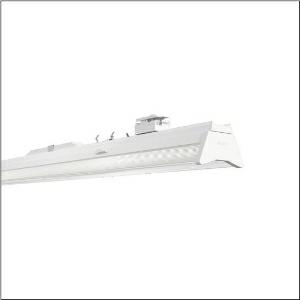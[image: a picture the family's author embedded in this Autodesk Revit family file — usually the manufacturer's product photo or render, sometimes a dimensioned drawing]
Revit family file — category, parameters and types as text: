
# Revit family: licross_r__11_performance_ho_51tm16cn4exm_9d3d
name_source: partatom
category: Lighting Fixtures
units: mm (PartAtom-declared; Revit-internal decimal feet)

## family parameters
Cut with Voids When Loaded = No
Host = Face
Light Source = No
Part Type = Normal
Room Calculation Point = No
Round Connector Dimension = Use Diameter
Shared = No

## types (1)
- --- (1 x LED, 14420 lm, 77.6 W, 4000K)
    Apparent Load = 78 VA
    CIE Flux Codes = 63 87 95 78 100
    Color Rendering = 80
    Color Temperature = 4000K
    Default Elevation = 1800 mm
    Description = Licross® 11 Performance HO, luminaire insert, of sheet steel, galvanised, coil coated, white, length: 1.500mm, width: 120mm, height: 123mm, LED rated luminous flux: 14.420lm, light colour: 840, control gear: ON/OFF Multilumen, CLOi, with plug, 3-pole, with phase selection, mains connection: 220..240V, AC, 50/60Hz, start of lifetime: 78W, end of service life: 87W, internal wiring halogen-free, primary light control with lens, of plastic, primary optical cover: cover, of PMMA, light emission: direct/indirect distribution, primary light characteristic: symmetric, protection rating (complete): IP40, insulation class (complete): insulation class I (protective earthing), certification: CE, ENEC, VDE, UKCA, protection symbol: D if used in an environment without relevant dust loads with corresponding accessories, impact resistance: IK06, permissible ambient temperature for indoor applications: -35..+35°C, corresponds to IFS (International Featured Standards) requirements for safety and quality in the food industry, reducing of maximum allowable ambient temperature of 5°C with ceiling mounting, LABS conformity tested according to VDMA 24364:2018-05, packaging unit: 1 piece
    Height = 114 mm
    Lamp = 1 x LED
    Lamp Light Flux = 14420 lm
    Lamp Power = 77.6 W
    Lamp count = 1
    Length = 1500 mm
    Luminous efficacy = 186 lm/W
    Manufacturer = Siteco
    ModVariant = No
    Model = 51TM16CN4EXM
    Mounting Place = Ceiling
    Mounting Type = Pendant
    Number of Poles = 1
    OnlyDefault = Yes
    Power Factor = 1
    Product Name = Licross® 11 Performance HO
    Product group = luminaire insert | ceiling pendant
    ProductGroupID = 902
    Protection Class = Protection class I
    Protection Degree = IP 40
    RLX_Detail_Level = 1
    RLX_Emergency_Light_Flux = 0 lm
    RLX_Emergency_Type = 0
    RLX_Emergency_Type_DB = No
    RlxData = <blob elided: 31933 chars, md5=3d173657>
    Socket = socket
    Standby Power = 0 W
    System Light Flux = 14420 lm
    System Power = 78 W
    Type Comments = factory setting: luminous flux: 100 % | (A | C | E) | 181 mA
    Type Image = l_1256138.jpg
    URL = http://relux.com
    VarID = @adj_107713
    Voltage = 0 V
    Weight = 0.00 kg
    Width = 120 mm

## geometry (parser evidence)
native form markers: Blend x4, Sweep x10
no freeform markers — native parametric forms only
